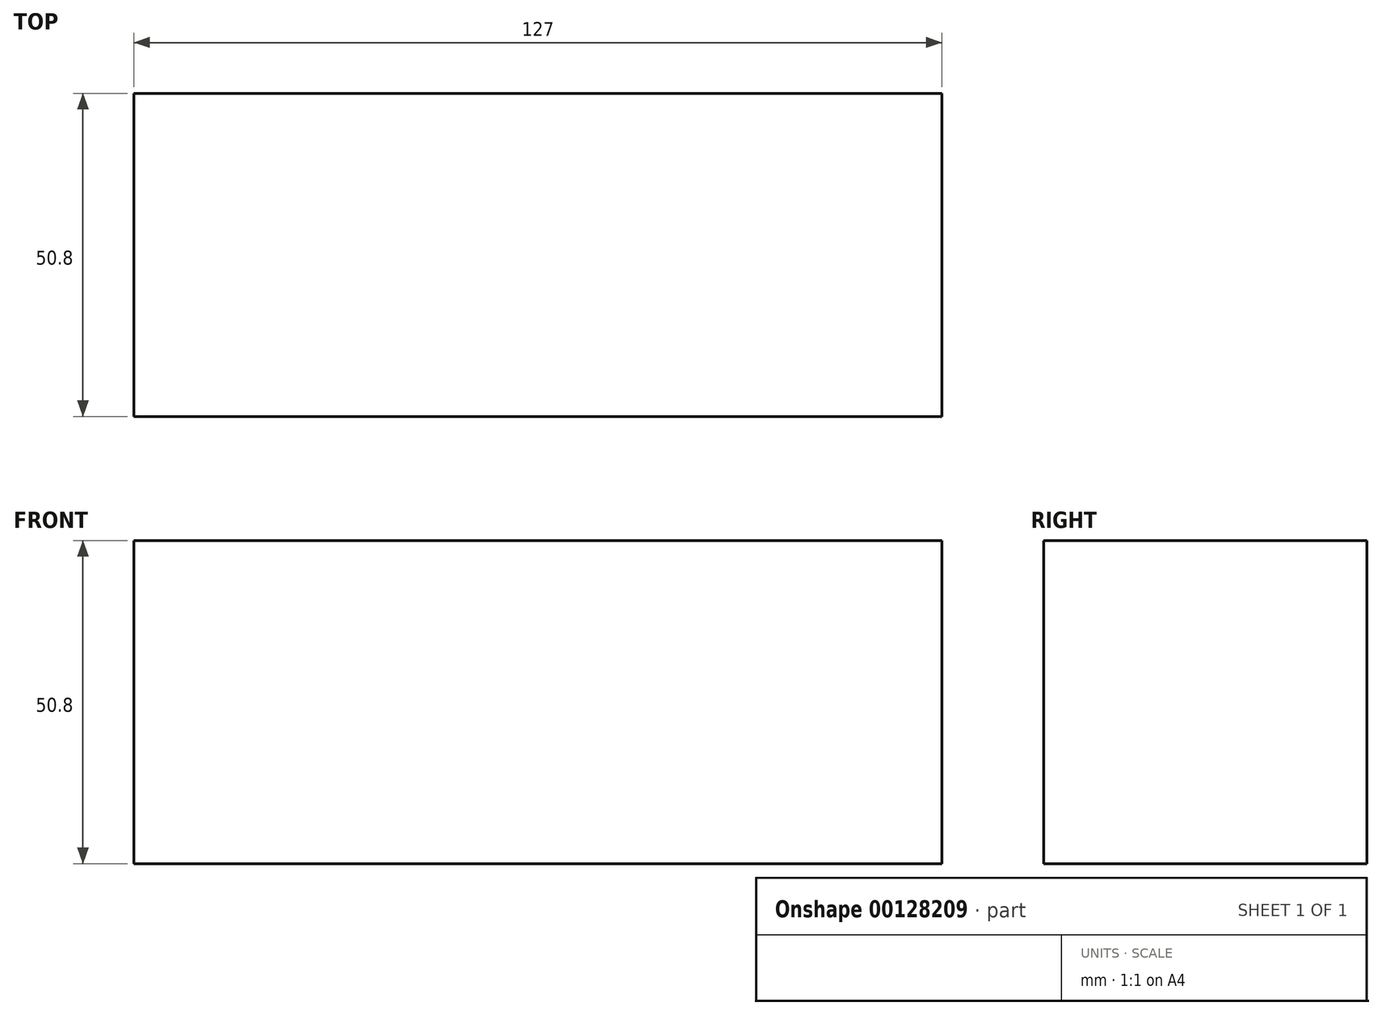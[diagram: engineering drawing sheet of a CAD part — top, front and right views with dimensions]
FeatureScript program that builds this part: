
annotation { "Feature Type Name" : "Feature", "Feature Type Description" : "" }
export const myFeature = defineFeature(function(context is Context, id is Id, definition is map)
    precondition{}
    {
        {
            var Q0;
            Q0=qCreatedBy(makeId("Front.planeOp"),FACE);
            var sketch = newSketch(context, id + "F0", { "sketchPlane" : qUnion([Q0])});
            skLineSegment(sketch, "E0.bottom", {"start": v(-146.07, -67.06) * mm, "end": v(-19.07, -67.06) * mm});
            skLineSegment(sketch, "E0.top", {"start": v(-146.07, -16.26) * mm, "end": v(-19.07, -16.26) * mm});
            skLineSegment(sketch, "E0.left", {"start": v(-146.07, -67.06) * mm, "end": v(-146.07, -16.26) * mm});
            skLineSegment(sketch, "E0.right", {"start": v(-19.07, -67.06) * mm, "end": v(-19.07, -16.26) * mm});
            skSolve(sketch);
        }
        {
            var Q0;
            Q0 = qSketchRegion(id + "F0", true);
            extrude(context, id + "F1", {"entities" : qUnion([Q0]), "depth" : 50.8 * mm});
        }
    });
